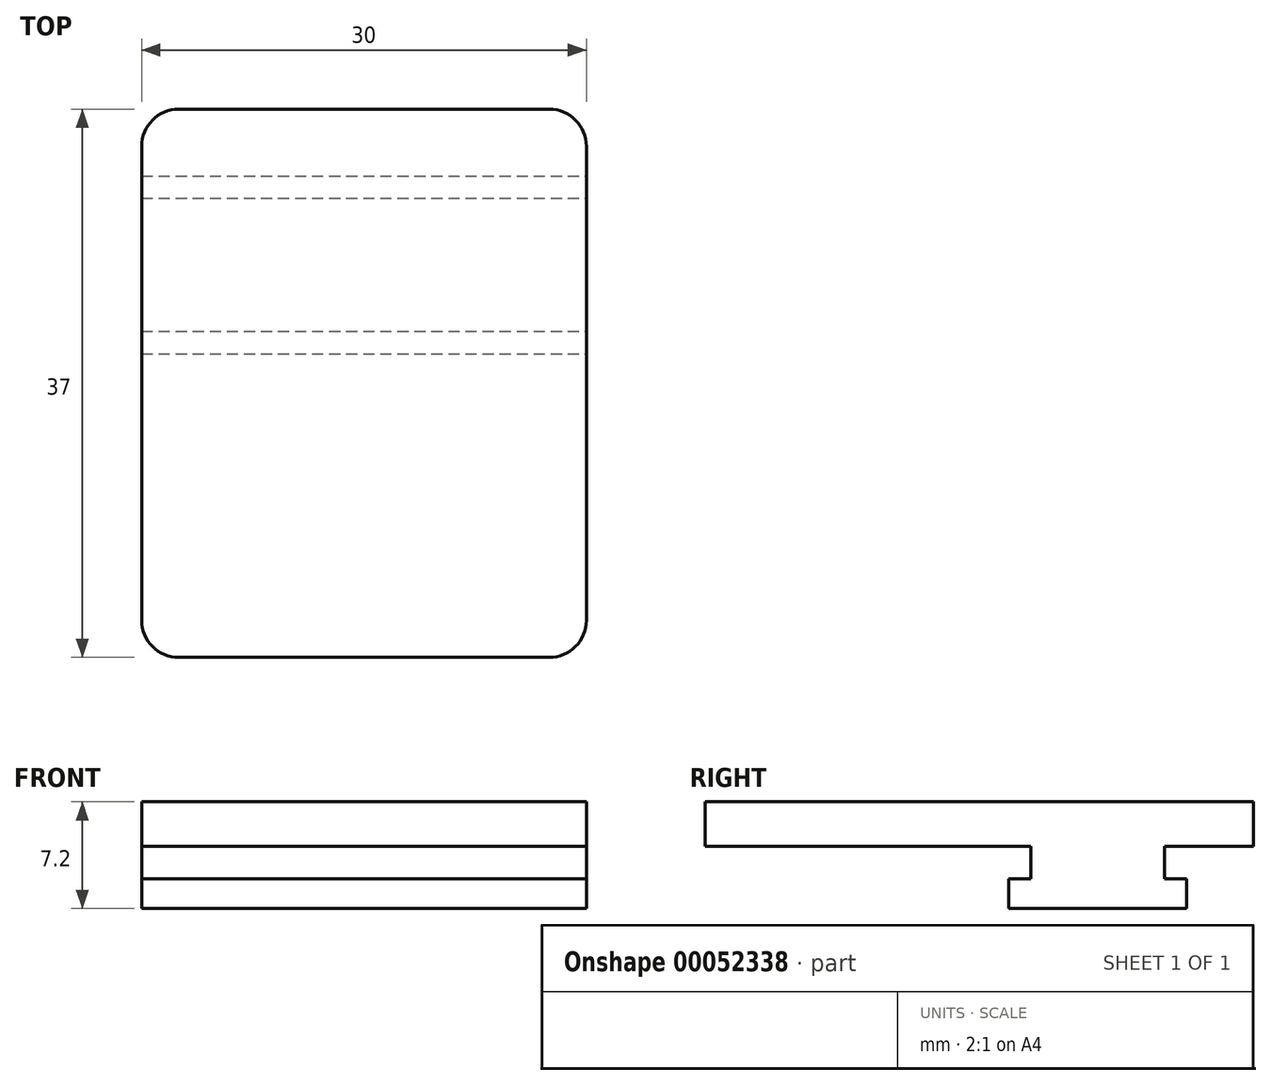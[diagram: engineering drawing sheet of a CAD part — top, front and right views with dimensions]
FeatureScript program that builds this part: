
annotation { "Feature Type Name" : "Feature", "Feature Type Description" : "" }
export const myFeature = defineFeature(function(context is Context, id is Id, definition is map)
    precondition{}
    {
        {
            var Q0;
            Q0=qCreatedBy(makeId("Top.planeOp"),FACE);
            var sketch = newSketch(context, id + "F0", { "sketchPlane" : qUnion([Q0])});
            skLineSegment(sketch, "E0.bottom", {"start": v(0, 0) * mm, "end": v(30, 0) * mm});
            skLineSegment(sketch, "E0.top", {"start": v(0, -12) * mm, "end": v(30, -12) * mm});
            skLineSegment(sketch, "E0.left", {"start": v(0, 0) * mm, "end": v(0, -12) * mm});
            skLineSegment(sketch, "E0.right", {"start": v(30, 0) * mm, "end": v(30, -12) * mm});
            skSolve(sketch);
        }
        {
            var Q0;
            Q0=makeQuery(id+"F0.imprint","IMPRINT",FACE,{"disambiguationData":[TD([[makeQuery(id+"F0.imprint","IMPRINT",EDGE,{"derivedFrom":sQuery(id+"F0.wireOp",EDGE,"E0.bottom")}),-1.0]])]});
            extrude(context, id + "F1", {"entities" : qUnion([Q0]), "depth" : 2 * mm});
        }
        {
            var Q0;
            Q0=makeQuery(id+"F1.opExtrude","CAP_FACE",FACE,{"disambiguationData":[OSD([sQuery(id+"F0.wireOp",EDGE,"E0.bottom"),sQuery(id+"F0.wireOp",EDGE,"E0.top"),sQuery(id+"F0.wireOp",EDGE,"E0.left"),sQuery(id+"F0.wireOp",EDGE,"E0.right")])],"isStart":false});
            var sketch = newSketch(context, id + "F2", { "sketchPlane" : qUnion([Q0])});
            skLineSegment(sketch, "E1.bottom", {"start": v(0, -1.5) * mm, "end": v(30, -1.5) * mm});
            skLineSegment(sketch, "E1.top", {"start": v(0, -10.5) * mm, "end": v(30, -10.5) * mm});
            skLineSegment(sketch, "E1.left", {"start": v(0, -1.5) * mm, "end": v(0, -10.5) * mm});
            skLineSegment(sketch, "E1.right", {"start": v(30, -1.5) * mm, "end": v(30, -10.5) * mm});
            skSolve(sketch);
        }
        {
            var Q0;
            Q0=makeQuery(id+"F2.imprint","IMPRINT",FACE,{"disambiguationData":[TD([[makeQuery(id+"F2.imprint","IMPRINT",EDGE,{"derivedFrom":sQuery(id+"F2.wireOp",EDGE,"E1.bottom")}),-1.0]])]});
            extrude(context, id + "F3", {"entities" : qUnion([Q0]), "operationType" : NewBodyOperationType.ADD, "depth" : 2.2 * mm});
        }
        {
            var Q0;
            Q0=makeQuery(id+"F3.opExtrude","CAP_FACE",FACE,{"disambiguationData":[OSD([sQuery(id+"F2.wireOp",EDGE,"E1.bottom"),sQuery(id+"F2.wireOp",EDGE,"E1.top"),sQuery(id+"F2.wireOp",EDGE,"E1.left"),sQuery(id+"F2.wireOp",EDGE,"E1.right")])],"isStart":false});
            var sketch = newSketch(context, id + "F4", { "sketchPlane" : qUnion([Q0])});
            skLineSegment(sketch, "E2.bottom", {"start": v(0, 4.5) * mm, "end": v(30, 4.5) * mm});
            skLineSegment(sketch, "E2.top", {"start": v(0, -32.5) * mm, "end": v(30, -32.5) * mm});
            skLineSegment(sketch, "E2.left", {"start": v(0, 4.5) * mm, "end": v(0, -32.5) * mm});
            skLineSegment(sketch, "E2.right", {"start": v(30, 4.5) * mm, "end": v(30, -32.5) * mm});
            skSolve(sketch);
        }
        {
            var Q0;
            {var subQ0=sQuery(id+"F4.wireOp",EDGE,"E2.top");Q0=makeQuery(id+"F4.imprint","IMPRINT",FACE,{"disambiguationData":[TD([[makeQuery(id+"F4.imprint","IMPRINT",EDGE,{"derivedFrom":subQ0}),1.0]])]});}
            var Q1;
            {var subQ1=makeQuery(id+"F3.opExtrude","CAP_EDGE",EDGE,{"disambiguationData":[OSD([sQuery(id+"F2.wireOp",EDGE,"E1.bottom")])],"isStart":false});Q1=makeQuery(id+"F4.imprint","IMPRINT",FACE,{"disambiguationData":[TD([[makeQuery(id+"F4.imprint","IMPRINT",EDGE,{"derivedFrom":subQ1}),-1.0]])]});}
            var Q2;
            {var subQ0=sQuery(id+"F4.wireOp",EDGE,"E2.bottom");Q2=makeQuery(id+"F4.imprint","IMPRINT",FACE,{"disambiguationData":[TD([[makeQuery(id+"F4.imprint","IMPRINT",EDGE,{"derivedFrom":subQ0}),-1.0]])]});}
            extrude(context, id + "F5", {"entities" : qUnion([Q0, Q1, Q2]), "operationType" : NewBodyOperationType.ADD, "depth" : 3 * mm});
        }
        {
            var Q0;
            Q0=makeQuery(id+"F5.opExtrude","SWEPT_EDGE",EDGE,{"disambiguationData":[OSD([sQuery(id+"F4.wireOp",EDGE,"E2.top"),sQuery(id+"F4.wireOp",EDGE,"E2.left")])]});
            var Q1;
            Q1=makeQuery(id+"F5.opExtrude","SWEPT_EDGE",EDGE,{"disambiguationData":[OSD([sQuery(id+"F4.wireOp",EDGE,"E2.top"),sQuery(id+"F4.wireOp",EDGE,"E2.right")])]});
            var Q2;
            Q2=makeQuery(id+"F5.opExtrude","SWEPT_EDGE",EDGE,{"disambiguationData":[OSD([sQuery(id+"F4.wireOp",EDGE,"E2.bottom"),sQuery(id+"F4.wireOp",EDGE,"E2.right")])]});
            var Q3;
            Q3=makeQuery(id+"F5.opExtrude","SWEPT_EDGE",EDGE,{"disambiguationData":[OSD([sQuery(id+"F4.wireOp",EDGE,"E2.bottom"),sQuery(id+"F4.wireOp",EDGE,"E2.left")])]});
            fillet(context, id + "F6", {"entities" : qUnion([Q0, Q1, Q2, Q3]), "radius" : 2.5 * mm, "tangentPropagation" : true, "allowEdgeOverflow" : false});
        }
    });
